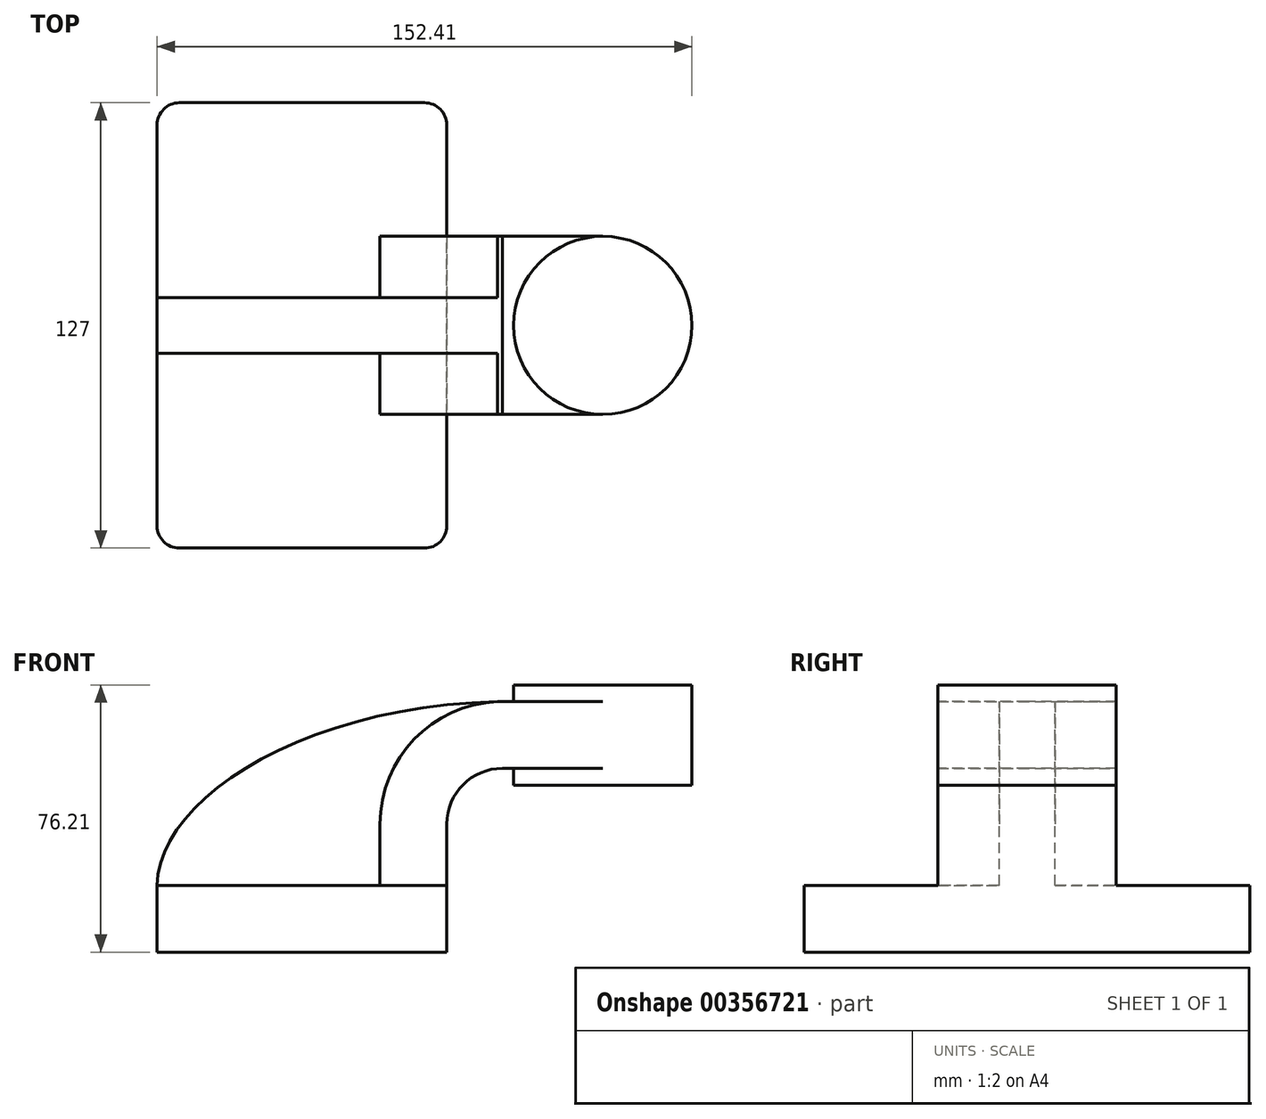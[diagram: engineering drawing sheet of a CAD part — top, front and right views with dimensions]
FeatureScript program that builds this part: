
annotation { "Feature Type Name" : "Feature", "Feature Type Description" : "" }
export const myFeature = defineFeature(function(context is Context, id is Id, definition is map)
    precondition{}
    {
        {
            var Q0;
            Q0=qCreatedBy(makeId("Front.planeOp"),FACE);
            var sketch = newSketch(context, id + "F0", { "sketchPlane" : qUnion([Q0])});
            skLineSegment(sketch, "E0.bottom", {"start": v(-41.28, -9.53) * mm, "end": v(41.28, -9.53) * mm});
            skLineSegment(sketch, "E0.top", {"start": v(-41.28, 9.52) * mm, "end": v(41.28, 9.52) * mm});
            skLineSegment(sketch, "E0.left", {"start": v(-41.28, -9.53) * mm, "end": v(-41.28, 9.53) * mm});
            skLineSegment(sketch, "E0.right", {"start": v(41.28, -9.53) * mm, "end": v(41.28, 9.52) * mm});
            skPoint(sketch, "E0.middle", {"position": v(0, 0) * mm});
            skLineSegment(sketch, "E1.bottom", {"start": v(60.32, 38.1) * mm, "end": v(111.12, 38.1) * mm});
            skLineSegment(sketch, "E1.top", {"start": v(60.32, 66.67) * mm, "end": v(111.12, 66.67) * mm});
            skLineSegment(sketch, "E1.left", {"start": v(60.32, 38.1) * mm, "end": v(60.32, 66.67) * mm});
            skLineSegment(sketch, "E1.right", {"start": v(111.12, 38.1) * mm, "end": v(111.12, 66.67) * mm});
            skPoint(sketch, "E1.middle", {"position": v(85.72, 52.39) * mm});
            skLineSegment(sketch, "E2", {"start": v(41.28, 9.52) * mm, "end": v(41.28, 27) * mm});
            skArc(sketch, "E3", {"start": v(41.27, 27) * mm, "mid": v(45.92, 38.23) * mm, "end": v(57.15, 42.88) * mm});
            skLineSegment(sketch, "E4", {"start": v(57.15, 42.88) * mm, "end": v(85.72, 42.88) * mm});
            skPoint(sketch, "E4.endSnap0", {"position": v(85.72, 38.1) * mm});
            skLineSegment(sketch, "E5.0", {"start": v(57.15, 61.93) * mm, "end": v(85.72, 61.93) * mm});
            skArc(sketch, "E5.1", {"start": v(22.22, 27) * mm, "mid": v(32.45, 51.7) * mm, "end": v(57.15, 61.93) * mm});
            skLineSegment(sketch, "E5.2", {"start": v(22.22, 9.52) * mm, "end": v(22.22, 27) * mm});
            skLineSegment(sketch, "E6", {"start": v(85.72, 38.1) * mm, "end": v(85.72, 42.88) * mm});
            skLineSegment(sketch, "E7", {"start": v(85.72, 42.88) * mm, "end": v(85.72, 52.39) * mm});
            skLineSegment(sketch, "E8", {"start": v(85.72, 52.39) * mm, "end": v(85.72, 61.93) * mm});
            skLineSegment(sketch, "E9", {"start": v(85.72, 61.93) * mm, "end": v(85.72, 66.67) * mm});
            skFitSpline(sketch, "E10", {"points": [v(-41.28, 9.53) * mm, v(57.15, 61.93) * mm], "startDerivative": vector(0.63, 72.83) * mm, "endDerivative": vector(171.45, 2.81) * mm});
            skSolve(sketch);
        }
        {
            var Q0;
            Q0=makeQuery(id+"F0.imprint","IMPRINT",FACE,{"disambiguationData":[TD([[makeQuery(id+"F0.imprint","IMPRINT",EDGE,{"derivedFrom":sQuery(id+"F0.wireOp",EDGE,"E0.bottom")}),1.0]])]});
            extrude(context, id + "F1", {"entities" : qUnion([Q0]), "endBound" : BoundingType.SYMMETRIC, "oppositeDirection" : true, "depth" : 127 * mm});
        }
        {
            var Q0;
            {var subQ1=sQuery(id+"F0.wireOp",EDGE,"E2");Q0=makeQuery(id+"F0.imprint","IMPRINT",FACE,{"disambiguationData":[TD([[makeQuery(id+"F0.imprint","IMPRINT",EDGE,{"derivedFrom":subQ1}),1.0]])]});}
            var Q1;
            {var subQ0=sQuery(id+"F0.wireOp",EDGE,"E7");Q1=makeQuery(id+"F0.imprint","IMPRINT",FACE,{"disambiguationData":[TD([[makeQuery(id+"F0.imprint","IMPRINT",EDGE,{"derivedFrom":subQ0}),1.0]])]});}
            extrude(context, id + "F2", {"entities" : qUnion([Q0, Q1]), "operationType" : NewBodyOperationType.ADD, "endBound" : BoundingType.SYMMETRIC, "depth" : 50.8 * mm});
        }
        {
            var Q0;
            {var subQ3=sQuery(id+"F0.wireOp",EDGE,"E5.2");Q0=makeQuery(id+"F0.imprint","IMPRINT",FACE,{"disambiguationData":[TD([[makeQuery(id+"F0.imprint","IMPRINT",EDGE,{"derivedFrom":subQ3}),1.0]])]});}
            extrude(context, id + "F3", {"entities" : qUnion([Q0]), "operationType" : NewBodyOperationType.ADD, "endBound" : BoundingType.SYMMETRIC, "depth" : 15.88 * mm});
        }
        {
            var Q0;
            {var subQ1=sQuery(id+"F0.wireOp",EDGE,"E1.right");Q0=makeQuery(id+"F0.imprint","IMPRINT",FACE,{"disambiguationData":[TD([[makeQuery(id+"F0.imprint","IMPRINT",EDGE,{"derivedFrom":subQ1}),1.0]])]});}
            var Q1;
            Q1=sQuery(id+"F0.wireOp",EDGE,"E8");
            revolve(context, id + "F4", {"operationType" : NewBodyOperationType.ADD, "entities" : qUnion([Q0]), "axis" : qUnion([Q1]), "revolveType" : RevolveType.FULL});
        }
        {
            var Q0;
            Q0=makeQuery(id+"F1.opExtrude","CAP_EDGE",EDGE,{"disambiguationData":[OSD([sQuery(id+"F0.wireOp",EDGE,"E0.right")])],"isStart":true});
            var Q1;
            Q1=makeQuery(id+"F1.opExtrude","CAP_EDGE",EDGE,{"disambiguationData":[OSD([sQuery(id+"F0.wireOp",EDGE,"E0.left")])],"isStart":true});
            var Q2;
            Q2=makeQuery(id+"F1.opExtrude","CAP_EDGE",EDGE,{"disambiguationData":[OSD([sQuery(id+"F0.wireOp",EDGE,"E0.right")])],"isStart":false});
            var Q3;
            Q3=makeQuery(id+"F1.opExtrude","CAP_EDGE",EDGE,{"disambiguationData":[OSD([sQuery(id+"F0.wireOp",EDGE,"E0.left")])],"isStart":false});
            fillet(context, id + "F5", {"entities" : qUnion([Q0, Q1, Q2, Q3]), "radius" : 6.35 * mm, "tangentPropagation" : true, "allowEdgeOverflow" : false});
        }
    });
